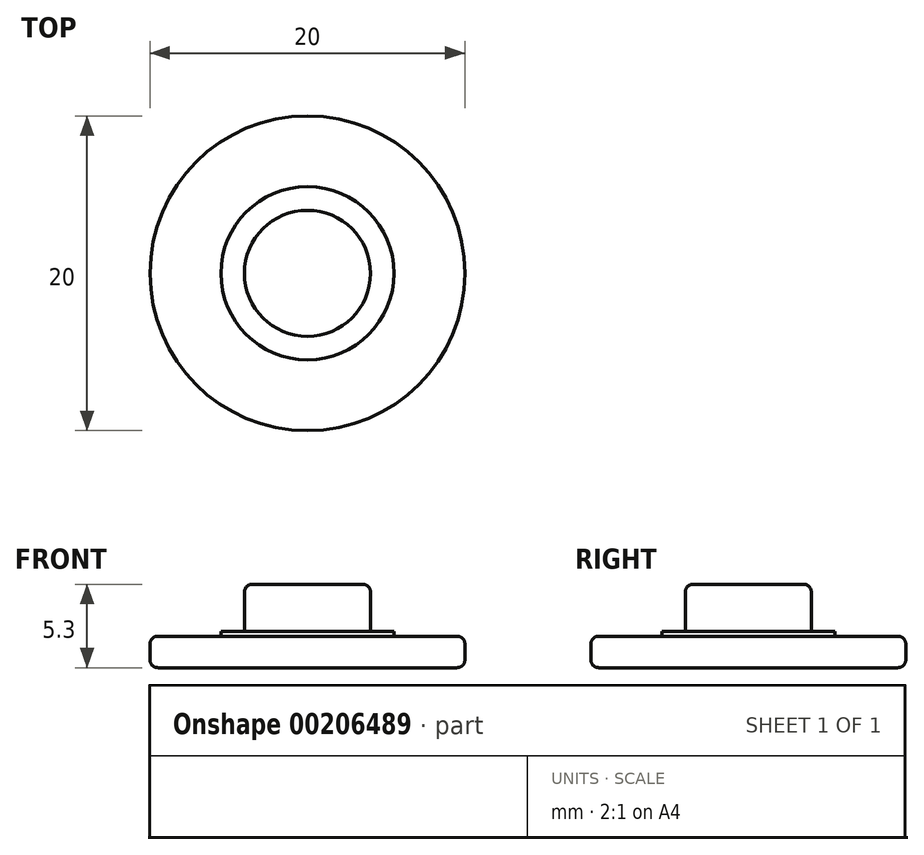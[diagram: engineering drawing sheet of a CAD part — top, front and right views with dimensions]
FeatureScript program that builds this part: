
annotation { "Feature Type Name" : "Feature", "Feature Type Description" : "" }
export const myFeature = defineFeature(function(context is Context, id is Id, definition is map)
    precondition{}
    {
        {
            var Q0;
            Q0=qCreatedBy(makeId("Top.planeOp"),FACE);
            var sketch = newSketch(context, id + "F0", { "sketchPlane" : qUnion([Q0])});
            skCircle(sketch, "E0", {"center": v(0, 0) * mm, "radius": 10 * mm});
            skSolve(sketch);
        }
        {
            var Q0;
            Q0=makeQuery(id+"F0.imprint","IMPRINT",FACE,{"disambiguationData":[TD([[makeQuery(id+"F0.imprint","IMPRINT",EDGE,{"derivedFrom":sQuery(id+"F0.wireOp",EDGE,"E0")}),1.0]])]});
            extrude(context, id + "F1", {"entities" : qUnion([Q0]), "depth" : 2 * mm, "offsetDistance" : 25 * mm});
        }
        {
            var Q0;
            Q0=makeQuery(id+"F1.opExtrude","CAP_FACE",FACE,{"disambiguationData":[OSD([sQuery(id+"F0.wireOp",EDGE,"E0")])],"isStart":false});
            var sketch = newSketch(context, id + "F2", { "sketchPlane" : qUnion([Q0])});
            skCircle(sketch, "E1", {"center": v(0, 0) * mm, "radius": 5.5 * mm});
            skSolve(sketch);
        }
        {
            var Q0;
            Q0=makeQuery(id+"F2.imprint","IMPRINT",FACE,{"disambiguationData":[TD([[makeQuery(id+"F2.imprint","IMPRINT",EDGE,{"derivedFrom":sQuery(id+"F2.wireOp",EDGE,"E1")}),1.0]])]});
            extrude(context, id + "F3", {"entities" : qUnion([Q0]), "operationType" : NewBodyOperationType.ADD, "depth" : 0.3 * mm, "offsetDistance" : 25 * mm});
        }
        {
            var Q0;
            Q0=makeQuery(id+"F3.opExtrude","CAP_FACE",FACE,{"disambiguationData":[OSD([sQuery(id+"F2.wireOp",EDGE,"E1")])],"isStart":false});
            var sketch = newSketch(context, id + "F4", { "sketchPlane" : qUnion([Q0])});
            skCircle(sketch, "E2", {"center": v(0, 0) * mm, "radius": 4 * mm});
            skSolve(sketch);
        }
        {
            var Q0;
            Q0 = qSketchRegion(id + "F4", true);
            extrude(context, id + "F5", {"entities" : qUnion([Q0]), "operationType" : NewBodyOperationType.ADD, "depth" : 3 * mm, "offsetDistance" : 25 * mm});
        }
        {
            var Q0;
            Q0=makeQuery(id+"F5.opExtrude","CAP_EDGE",EDGE,{"disambiguationData":[OSD([sQuery(id+"F4.wireOp",EDGE,"E2")])],"isStart":false});
            var Q1;
            Q1=makeQuery(id+"F1.opExtrude","CAP_EDGE",EDGE,{"disambiguationData":[OSD([sQuery(id+"F0.wireOp",EDGE,"E0")])],"isStart":false});
            var Q2;
            Q2=makeQuery(id+"F1.opExtrude","CAP_EDGE",EDGE,{"disambiguationData":[OSD([sQuery(id+"F0.wireOp",EDGE,"E0")])],"isStart":true});
            fillet(context, id + "F6", {"entities" : qUnion([Q0, Q1, Q2]), "radius" : 0.5 * mm, "tangentPropagation" : true, "allowEdgeOverflow" : false});
        }
    });
